# Revit family: 9650
name_source: partatom
category: Plumbing Fixtures
revit_build: Autodesk Revit 2014 (Build: 20130308_1515(x64)
units: mm (PartAtom-declared; Revit-internal decimal feet)

## types (5) — shared parameters
CW Connection = Yes
Description = General Purpose P-Trap
HW Connection = Yes
Manufacturer = Jay R Smith
Material = Metal-Jay R Smith-Type 304-Stainless Steel
Product Documentation Link = https://www.jrsmith.com
Product Page URL = https://www.jrsmith.com
URL = http://www.jrsmith.com
Vent Connection = No
Waste Connection = Yes
Width = 8"
zero-valued in all types: CWFU, HWFU, WFU

## per-type parameters (varying)
| type | B - Length | C - Height | Connection Radius | Connection Size | D - Nominal Height | Nominal Height 2 | Nominal Length |
| 9650BW02-S10 | 12" | 8 3/8" | 1" | 2" | 7 3/16" | 18 17/32" | 5" |
| 9650BW03-S10 | 19 1/2" | 12 1/2" | 1 1/2" | 3" | 12 1/4" | 18 17/32" | 8" |
| 9650BW04-S10 | 24" | 16 1/2" | 2" | 4" | 14 1/4" | 18 17/32" | 10" |
| 9650BW06-S10 | 33" | 24 5/8" | 3" | 6" | 21 5/16" | 18 17/32" | 13" |
| 9650BW08-S10 | 42" | 32 5/8" | 4" | 8" | 22 5/16" | 12 1/8" | 18" |

note: column(s) folded — value = type name in every type: Model

## geometry (parser evidence)
native form markers: Sweep x3
no freeform markers — native parametric forms only
